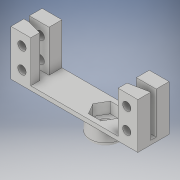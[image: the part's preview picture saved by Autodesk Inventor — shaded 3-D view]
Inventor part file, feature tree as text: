
AUTODESK INVENTOR PART (.ipt)
format: ipt  version: 2019 (Build 230136000, 136)  size: 204,288 bytes
history: native  units: mm
features: sketch x6, extrude x5, fillet x1
ambient origin geometry x8: Origin, YZ Plane, XZ Plane, XY Plane, X Axis, Y Axis, Z Axis, Center Point
bodies: Solide1 (feature_tree)
feature tree (12):
  extrude  "Extrusion1"  Depth=15.0mm
  extrude  "Extrusion2"  Depth=61.0mm
  extrude  "Extrusion3"  Depth=2.0mm TaperAngle=0.0deg
  sketch  "Esquisse4"
  sketch  "Esquisse5"
  extrude  "Extrusion6"  Depth=20.0mm TaperAngle=0.0deg
  extrude  "Extrusion7"  Depth=4.0mm
  fillet  "Congé1"  Radius=4.2mm
  sketch  "Esquisse1"
  sketch  "Esquisse2"
  sketch  "Esquisse3"
  sketch  "Esquisse7"
